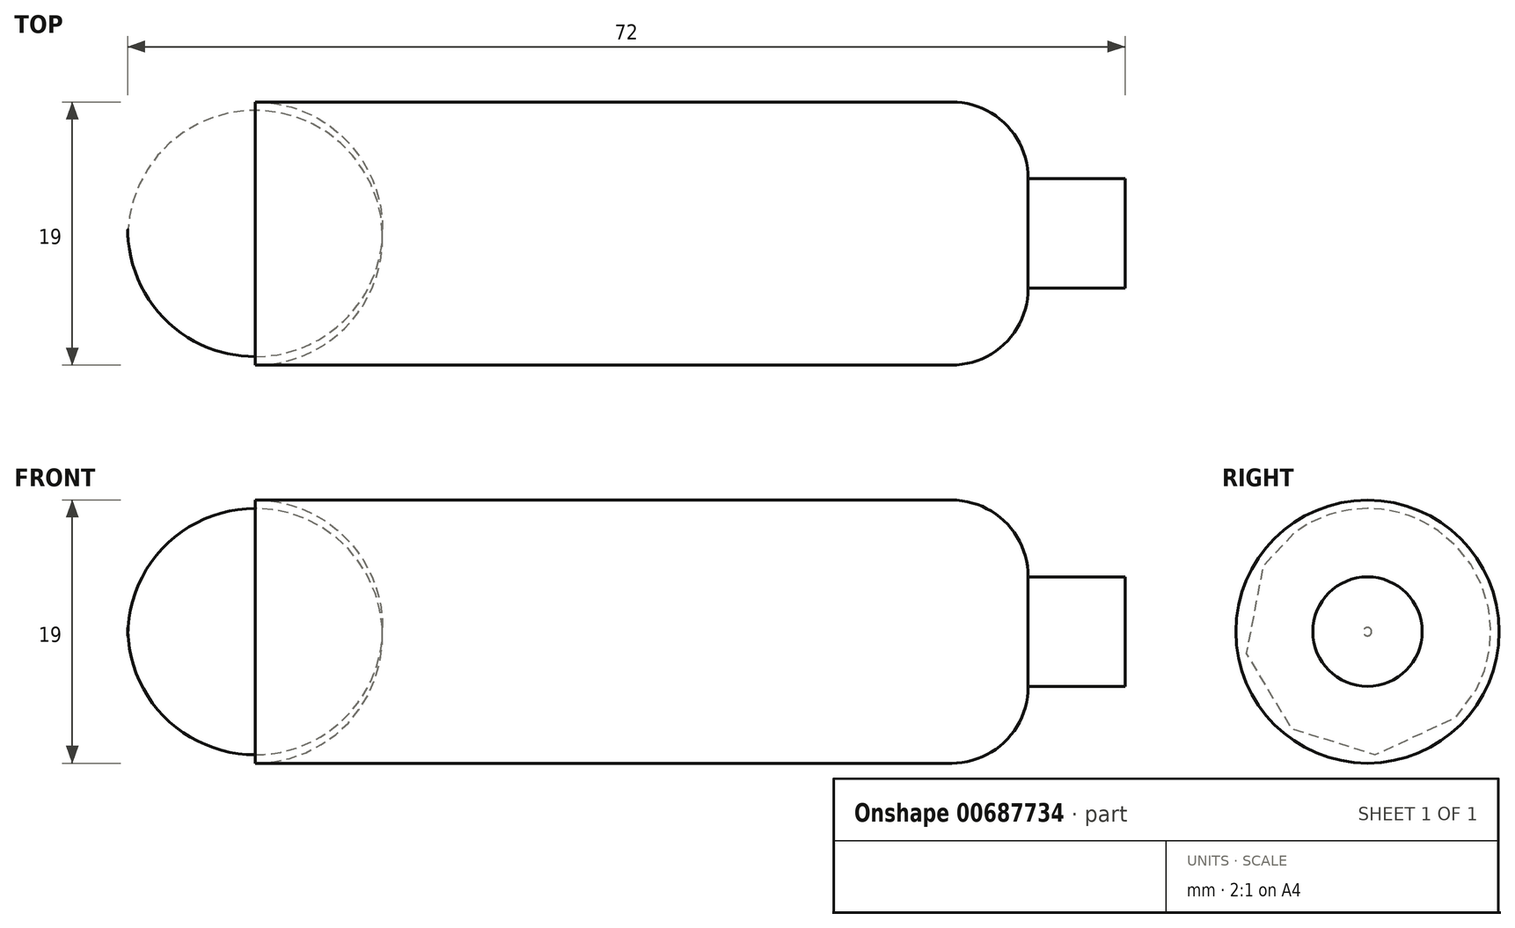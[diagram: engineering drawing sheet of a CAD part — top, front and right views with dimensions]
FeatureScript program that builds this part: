
annotation { "Feature Type Name" : "Feature", "Feature Type Description" : "" }
export const myFeature = defineFeature(function(context is Context, id is Id, definition is map)
    precondition{}
    {
        {
            var Q0;
            Q0=qCreatedBy(makeId("Right.planeOp"),FACE);
            var sketch = newSketch(context, id + "F0", { "sketchPlane" : qUnion([Q0])});
            skCircle(sketch, "E0", {"center": v(0, 0) * mm, "radius": 9.5 * mm});
            skSolve(sketch);
        }
        {
            var Q0;
            Q0=makeQuery(id+"F0.imprint","IMPRINT",FACE,{"disambiguationData":[TD([[makeQuery(id+"F0.imprint","IMPRINT",EDGE,{"derivedFrom":sQuery(id+"F0.wireOp",EDGE,"E0")}),1.0]])]});
            extrude(context, id + "F1", {"entities" : qUnion([Q0]), "depth" : 65 * mm, "offsetDistance" : 25.4 * mm});
        }
        {
            var Q0;
            Q0=makeQuery(id+"F1.opExtrude","CAP_FACE",FACE,{"disambiguationData":[OSD([sQuery(id+"F0.wireOp",EDGE,"E0")])],"isStart":true});
            fillet(context, id + "F2", {"entities" : qUnion([Q0]), "radius" : 9.2 * mm, "tangentPropagation" : true, "allowEdgeOverflow" : false});
        }
        {
            var Q0;
            Q0=makeQuery(id+"F1.opExtrude","CAP_FACE",FACE,{"disambiguationData":[OSD([sQuery(id+"F0.wireOp",EDGE,"E0")])],"isStart":false});
            fillet(context, id + "F3", {"entities" : qUnion([Q0]), "radius" : 5.52 * mm, "tangentPropagation" : true, "allowEdgeOverflow" : false});
        }
        {
            var Q0;
            Q0=makeQuery(id+"F1.opExtrude","CAP_FACE",FACE,{"disambiguationData":[OSD([sQuery(id+"F0.wireOp",EDGE,"E0")])],"isStart":false});
            var sketch = newSketch(context, id + "F4", { "sketchPlane" : qUnion([Q0])});
            skCircle(sketch, "E1", {"center": v(0, 0) * mm, "radius": 3.95 * mm});
            skSolve(sketch);
        }
        {
            var Q0;
            Q0=makeQuery(id+"F4.imprint","IMPRINT",FACE,{"disambiguationData":[TD([[makeQuery(id+"F4.imprint","IMPRINT",EDGE,{"derivedFrom":sQuery(id+"F4.wireOp",EDGE,"E1")}),1.0]])]});
            extrude(context, id + "F5", {"entities" : qUnion([Q0]), "operationType" : NewBodyOperationType.ADD, "depth" : 7 * mm, "offsetDistance" : 25.4 * mm});
        }
    });
